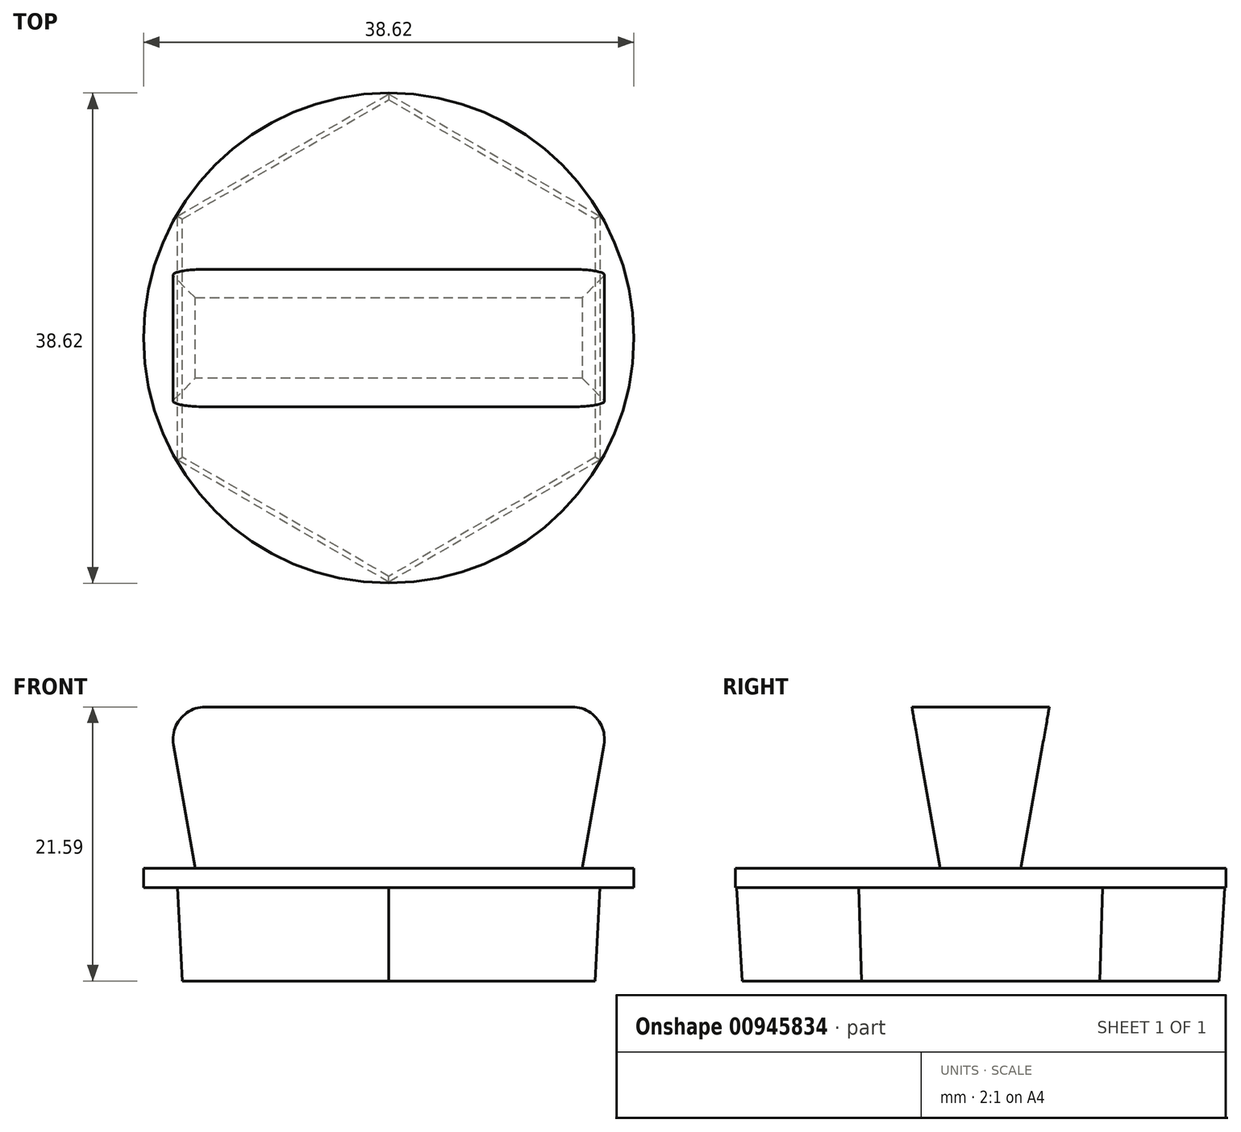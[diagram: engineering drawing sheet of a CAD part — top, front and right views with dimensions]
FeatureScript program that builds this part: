
annotation { "Feature Type Name" : "Feature", "Feature Type Description" : "" }
export const myFeature = defineFeature(function(context is Context, id is Id, definition is map)
    precondition{}
    {
        {
            var Q0;
            Q0=qCreatedBy(makeId("Top.planeOp"),FACE);
            var sketch = newSketch(context, id + "F0", { "sketchPlane" : qUnion([Q0])});
            skLineSegment(sketch, "E0", {"start": v(16.26, 9.39) * mm, "end": v(16.26, -9.39) * mm});
            skLineSegment(sketch, "E1", {"start": v(16.26, -9.39) * mm, "end": v(0, -18.77) * mm});
            skLineSegment(sketch, "E2", {"start": v(0, -18.77) * mm, "end": v(-16.26, -9.39) * mm});
            skLineSegment(sketch, "E3", {"start": v(-16.26, -9.39) * mm, "end": v(-16.26, 9.39) * mm});
            skLineSegment(sketch, "E4", {"start": v(-16.26, 9.39) * mm, "end": v(0, 18.77) * mm});
            skLineSegment(sketch, "E5", {"start": v(0, 18.77) * mm, "end": v(16.26, 9.39) * mm});
            skPoint(sketch, "E6", {"position": v(-16.26, 0) * mm});
            skPoint(sketch, "E7", {"position": v(16.26, 0) * mm});
            skLineSegment(sketch, "E8", {"start": v(-16.26, 0) * mm, "end": v(16.26, 0) * mm, "construction": true});
            skSolve(sketch);
        }
        {
            var Q0;
            Q0 = qSketchRegion(id + "F0", true);
            extrude(context, id + "F1", {"entities" : qUnion([Q0]), "depth" : 8.9 * mm, "offsetDistance" : 25.4 * mm, "hasDraft" : true, "draftAngle" : 3 * degree});
        }
        {
            var Q0;
            Q0=makeQuery(id+"F1.opExtrude","CAP_FACE",FACE,{"disambiguationData":[OSD([sQuery(id+"F0.wireOp",EDGE,"E0"),sQuery(id+"F0.wireOp",EDGE,"E1"),sQuery(id+"F0.wireOp",EDGE,"E2"),sQuery(id+"F0.wireOp",EDGE,"E3"),sQuery(id+"F0.wireOp",EDGE,"E4"),sQuery(id+"F0.wireOp",EDGE,"E5")])],"isStart":false});
            var sketch = newSketch(context, id + "F2", { "sketchPlane" : qUnion([Q0])});
            skCircle(sketch, "E9", {"center": v(0, 0) * mm, "radius": 19.3 * mm});
            skSolve(sketch);
        }
        {
            var Q0;
            Q0 = qSketchRegion(id + "F2", true);
            var Q1;
            Q1=sQuery(id+"F2.wireOp",EDGE,"E9");
            extrude(context, id + "F3", {"entities" : qUnion([Q0]), "operationType" : NewBodyOperationType.ADD, "surfaceEntities" : qUnion([Q1]), "oppositeDirection" : true, "depth" : 1.52 * mm, "offsetDistance" : 25.4 * mm});
        }
        {
            var Q0;
            Q0=makeQuery(id+"F3.boolean.opBoolean","MERGE",FACE,{"derivedFrom":[makeQuery(id+"F1.opExtrude","CAP_FACE",FACE,{"disambiguationData":[OSD([sQuery(id+"F0.wireOp",EDGE,"E0"),sQuery(id+"F0.wireOp",EDGE,"E1"),sQuery(id+"F0.wireOp",EDGE,"E2"),sQuery(id+"F0.wireOp",EDGE,"E3"),sQuery(id+"F0.wireOp",EDGE,"E4"),sQuery(id+"F0.wireOp",EDGE,"E5")])],"isStart":false}),makeQuery(id+"F3.opExtrude","CAP_FACE",FACE,{"disambiguationData":[OSD([sQuery(id+"F2.wireOp",EDGE,"E9")])],"isStart":true})]});
            var sketch = newSketch(context, id + "F4", { "sketchPlane" : qUnion([Q0])});
            skLineSegment(sketch, "E10.bottom", {"start": v(15.24, -3.17) * mm, "end": v(-15.24, -3.18) * mm});
            skLineSegment(sketch, "E10.top", {"start": v(15.24, 3.18) * mm, "end": v(-15.24, 3.17) * mm});
            skLineSegment(sketch, "E10.left", {"start": v(15.24, -3.17) * mm, "end": v(15.24, 3.18) * mm});
            skLineSegment(sketch, "E10.right", {"start": v(-15.24, -3.18) * mm, "end": v(-15.24, 3.17) * mm});
            skPoint(sketch, "E10.middle", {"position": v(0, 0) * mm});
            skSolve(sketch);
        }
        {
            var Q0;
            Q0 = qSketchRegion(id + "F4", true);
            extrude(context, id + "F5", {"entities" : qUnion([Q0]), "operationType" : NewBodyOperationType.ADD, "depth" : 12.7 * mm, "offsetDistance" : 25.4 * mm, "hasDraft" : true, "draftAngle" : 10 * degree});
        }
        {
            var Q0;
            Q0=makeQuery(id+"F5.opExtrude","CAP_EDGE",EDGE,{"disambiguationData":[OSD([sQuery(id+"F4.wireOp",EDGE,"E10.top")])],"isStart":true});
            var Q1;
            Q1=makeQuery(id+"F5.opExtrude","CAP_EDGE",EDGE,{"disambiguationData":[OSD([sQuery(id+"F4.wireOp",EDGE,"E10.right")])],"isStart":true});
            var Q2;
            Q2=makeQuery(id+"F5.opExtrude","CAP_EDGE",EDGE,{"disambiguationData":[OSD([sQuery(id+"F4.wireOp",EDGE,"E10.bottom")])],"isStart":true});
            var Q3;
            Q3=makeQuery(id+"F5.opExtrude","CAP_EDGE",EDGE,{"disambiguationData":[OSD([sQuery(id+"F4.wireOp",EDGE,"E10.left")])],"isStart":true});
            var Q4;
            Q4=makeQuery(id+"F5.opExtrude","CAP_EDGE",EDGE,{"disambiguationData":[OSD([sQuery(id+"F4.wireOp",EDGE,"E10.right")])],"isStart":false});
            var Q5;
            Q5=makeQuery(id+"F5.opExtrude","CAP_EDGE",EDGE,{"disambiguationData":[OSD([sQuery(id+"F4.wireOp",EDGE,"E10.left")])],"isStart":false});
            fillet(context, id + "F6", {"entities" : qUnion([Q0, Q1, Q2, Q3, Q4, Q5]), "radius" : 2.54 * mm, "tangentPropagation" : true, "allowEdgeOverflow" : false});
        }
    });
